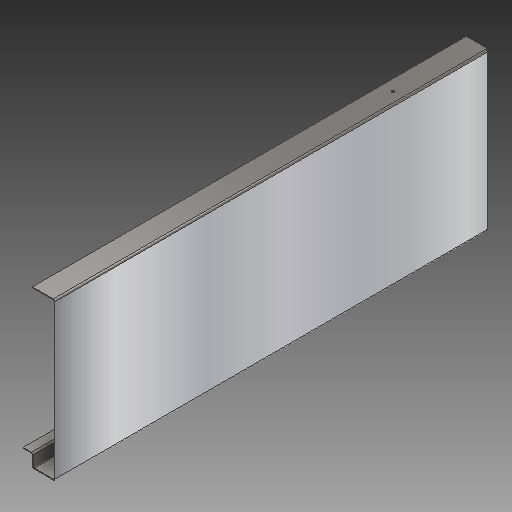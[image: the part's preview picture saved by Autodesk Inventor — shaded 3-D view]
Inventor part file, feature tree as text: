
AUTODESK INVENTOR PART (.ipt)
format: ipt  version: 2017 (Build 210142000, 142)  size: 282,624 bytes
history: native  units: in
note: dims shown in document units (in); Inventor stores cm internally (conversion verified against a paired STEP export)
features: other x6, sketch x3, plane x1
ambient origin geometry x8: Origin, YZ Plane, XZ Plane, XY Plane, X Axis, Y Axis, Z Axis, Center Point
bodies: Solid1 (feature_tree)
feature tree (10):
  other  "Lateral -A.ipt"
  plane  "Work Plane1"
  other  "Decal1"
  other  "Solid1::Lateral -A.ipt"
  other  "TaggingFeature1"
  sketch  "Sketch1"  dims[d0=0.3937in]
  sketch  "Sketch2"  dims[d1=7.874in]
  sketch  "Sketch3"
  other  "Image1"
  other  "Definition1"
